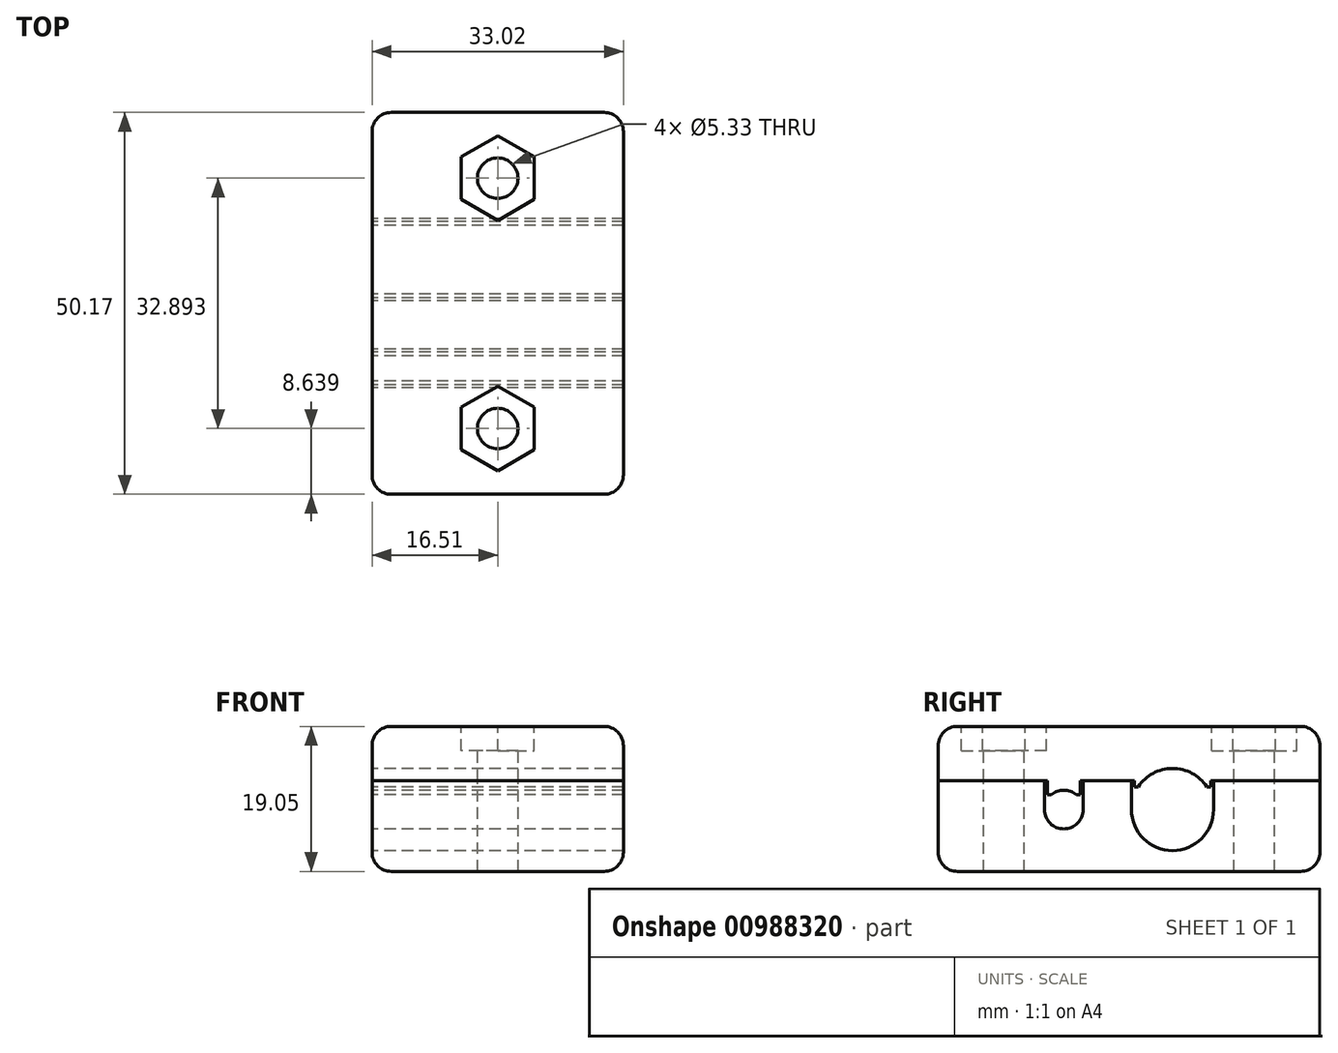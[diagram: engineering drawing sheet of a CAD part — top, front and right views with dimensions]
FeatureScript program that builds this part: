
annotation { "Feature Type Name" : "Feature", "Feature Type Description" : "" }
export const myFeature = defineFeature(function(context is Context, id is Id, definition is map)
    precondition{}
    {
        {
            var Q0;
            Q0=qCreatedBy(makeId("Right.planeOp"),FACE);
            var sketch = newSketch(context, id + "F0", { "sketchPlane" : qUnion([Q0])});
            skLineSegment(sketch, "E0", {"start": v(0, 10.92) * mm, "end": v(-30.8, 10.92) * mm});
            skLineSegment(sketch, "E1", {"start": v(-30.8, -8.13) * mm, "end": v(0, -8.13) * mm});
            skLineSegment(sketch, "E2", {"start": v(-30.8, 3.8) * mm, "end": v(-16.45, 3.8) * mm});
            skLineSegment(sketch, "E3", {"start": v(19.37, 3.81) * mm, "end": v(19.37, 10.92) * mm});
            skLineSegment(sketch, "E4", {"start": v(0, 10.92) * mm, "end": v(19.37, 10.92) * mm});
            skLineSegment(sketch, "E5", {"start": v(19.37, -8.13) * mm, "end": v(0, -8.13) * mm});
            skArc(sketch, "E6.trimOffspring", {"start": v(-5.4, 0) * mm, "mid": v(0, -5.4) * mm, "end": v(5.4, 0) * mm});
            skArc(sketch, "E7", {"start": v(-16.83, 0) * mm, "mid": v(-14.29, -2.54) * mm, "end": v(-11.75, 0) * mm});
            skLineSegment(sketch, "E8", {"start": v(5.4, 0) * mm, "end": v(5.4, 3.78) * mm});
            skLineSegment(sketch, "E9", {"start": v(5.4, 3.78) * mm, "end": v(19.37, 3.78) * mm});
            skLineSegment(sketch, "E10", {"start": v(19.37, 3.78) * mm, "end": v(19.37, -8.13) * mm});
            skLineSegment(sketch, "E11", {"start": v(-11.75, 0) * mm, "end": v(-11.75, 3.78) * mm});
            skLineSegment(sketch, "E12", {"start": v(-11.75, 3.78) * mm, "end": v(-5.4, 3.78) * mm});
            skLineSegment(sketch, "E13", {"start": v(-5.4, 3.78) * mm, "end": v(-5.4, 0) * mm});
            skLineSegment(sketch, "E14", {"start": v(-30.8, -8.13) * mm, "end": v(-30.8, 3.78) * mm});
            skLineSegment(sketch, "E15", {"start": v(-16.83, 0) * mm, "end": v(-16.83, 3.78) * mm});
            skLineSegment(sketch, "E16", {"start": v(-16.83, 3.78) * mm, "end": v(-30.8, 3.78) * mm});
            skLineSegment(sketch, "E17", {"start": v(-16.45, 3.8) * mm, "end": v(-16.45, 1.93) * mm});
            skLineSegment(sketch, "E18", {"start": v(-12.13, 1.93) * mm, "end": v(-12.13, 3.81) * mm});
            skLineSegment(sketch, "E19", {"start": v(-30.8, 3.8) * mm, "end": v(-30.8, 10.92) * mm});
            skLineSegment(sketch, "E20.trimOffspring", {"start": v(-12.13, 3.81) * mm, "end": v(-5.02, 3.81) * mm});
            skLineSegment(sketch, "E21.left", {"start": v(5.02, 3.81) * mm, "end": v(5.02, 3) * mm});
            skLineSegment(sketch, "E22.left", {"start": v(-5.02, 3.81) * mm, "end": v(-5.02, 3) * mm});
            skLineSegment(sketch, "E23.trimOffspring", {"start": v(5.02, 3.81) * mm, "end": v(19.37, 3.81) * mm});
            skLineSegment(sketch, "E24", {"start": v(5.02, 3) * mm, "end": v(4.5, 3) * mm});
            skLineSegment(sketch, "E25", {"start": v(-5.02, 3) * mm, "end": v(-4.5, 3) * mm});
            skArc(sketch, "E26", {"start": v(4.5, 3) * mm, "mid": v(0, 5.41) * mm, "end": v(-4.5, 3) * mm});
            skLineSegment(sketch, "E27", {"start": v(-12.13, 1.93) * mm, "end": v(-12.64, 1.93) * mm});
            skLineSegment(sketch, "E28", {"start": v(-16.45, 1.93) * mm, "end": v(-15.94, 1.93) * mm});
            skArc(sketch, "E29", {"start": v(-12.64, 1.93) * mm, "mid": v(-14.29, 2.54) * mm, "end": v(-15.94, 1.93) * mm});
            skSolve(sketch);
        }
        {
            var Q0;
            Q0=qSketchRegion(id+"F0",true);
            extrude(context, id + "F1", {"entities" : qUnion([Q0]), "depth" : 33.02 * mm, "offsetDistance" : 25.4 * mm});
        }
        {
            var Q0;
            Q0=makeQuery(id+"F1.opExtrude","SWEPT_FACE",FACE,{"disambiguationData":[OSD([sQuery(id+"F0.wireOp",EDGE,"E0"),sQuery(id+"F0.wireOp",EDGE,"E4")])]});
            var sketch = newSketch(context, id + "F2", { "sketchPlane" : qUnion([Q0])});
            skCircle(sketch, "E30", {"center": v(16.51, -22.16) * mm, "radius": 2.67 * mm});
            skPoint(sketch, "E30.centerSnap0", {"position": v(16.51, 19.37) * mm});
            skCircle(sketch, "E31", {"center": v(16.51, 10.73) * mm, "radius": 2.67 * mm});
            skSolve(sketch);
        }
        {
            var Q0;
            Q0=qSketchRegion(id+"F2",true);
            extrude(context, id + "F3", {"entities" : qUnion([Q0]), "operationType" : NewBodyOperationType.REMOVE, "oppositeDirection" : true, "depth" : 25.4 * mm, "offsetDistance" : 25.4 * mm});
        }
        {
            var Q0;
            Q0=makeQuery(id+"F1.opExtrude","SWEPT_FACE",FACE,{"disambiguationData":[OSD([sQuery(id+"F0.wireOp",EDGE,"E0"),sQuery(id+"F0.wireOp",EDGE,"E4")])]});
            var sketch = newSketch(context, id + "F4", { "sketchPlane" : qUnion([Q0])});
            skCircle(sketch, "E32.cCircle", {"center": v(16.51, -22.16) * mm, "radius": 4.83 * mm, "construction": true});
            skLineSegment(sketch, "E32.0", {"start": v(21.34, -19.38) * mm, "end": v(21.34, -24.95) * mm});
            skLineSegment(sketch, "E32.1", {"start": v(21.34, -24.95) * mm, "end": v(16.51, -27.73) * mm});
            skLineSegment(sketch, "E32.2", {"start": v(16.5, -27.73) * mm, "end": v(11.68, -24.95) * mm});
            skLineSegment(sketch, "E32.3", {"start": v(11.68, -24.95) * mm, "end": v(11.68, -19.38) * mm});
            skLineSegment(sketch, "E32.4", {"start": v(11.68, -19.38) * mm, "end": v(16.5, -16.59) * mm});
            skLineSegment(sketch, "E32.5", {"start": v(16.51, -16.59) * mm, "end": v(21.34, -19.38) * mm});
            skPoint(sketch, "E32.0.midPoint", {"position": v(21.34, -22.16) * mm});
            skLineSegment(sketch, "E33", {"start": v(33.02, -5.72) * mm, "end": v(5.36, -5.72) * mm, "construction": true});
            skPoint(sketch, "E34.MirrorP", {"position": v(21.34, 10.73) * mm});
            skLineSegment(sketch, "E35.MirrorCS", {"start": v(16.5, 16.3) * mm, "end": v(11.68, 13.52) * mm});
            skCircle(sketch, "E36.MirrorC", {"center": v(16.51, 10.73) * mm, "radius": 4.83 * mm, "construction": true});
            skLineSegment(sketch, "E37.MirrorCS", {"start": v(16.51, 5.16) * mm, "end": v(21.34, 7.95) * mm});
            skLineSegment(sketch, "E38.MirrorCS", {"start": v(11.68, 7.95) * mm, "end": v(16.5, 5.16) * mm});
            skLineSegment(sketch, "E39.MirrorCS", {"start": v(21.34, 7.95) * mm, "end": v(21.34, 13.52) * mm});
            skLineSegment(sketch, "E40.MirrorCS", {"start": v(21.34, 13.52) * mm, "end": v(16.5, 16.3) * mm});
            skLineSegment(sketch, "E41.MirrorCS", {"start": v(11.68, 13.52) * mm, "end": v(11.68, 7.95) * mm});
            skSolve(sketch);
        }
        {
            var Q0;
            Q0=qSketchRegion(id+"F4",true);
            extrude(context, id + "F5", {"entities" : qUnion([Q0]), "operationType" : NewBodyOperationType.REMOVE, "oppositeDirection" : true, "depth" : 3.17 * mm, "offsetDistance" : 25.4 * mm});
        }
        {
            var Q0;
            Q0=makeQuery(id+"F1.opExtrude","SWEPT_EDGE",EDGE,{"disambiguationData":[OSD([sQuery(id+"F0.wireOp",EDGE,"RtNWUVL0-efdT-tvqy-NiaK-mgzKuhDWmYlO"),sQuery(id+"F0.wireOp",EDGE,"E5")])]});
            var Q1;
            Q1=makeQuery(id+"F1.opExtrude","SWEPT_EDGE",EDGE,{"disambiguationData":[OSD([sQuery(id+"F0.wireOp",EDGE,"E3"),sQuery(id+"F0.wireOp",EDGE,"E4")])]});
            var Q2;
            Q2=makeQuery(id+"F1.opExtrude","CAP_EDGE",EDGE,{"disambiguationData":[OSD([sQuery(id+"F0.wireOp",EDGE,"E0"),sQuery(id+"F0.wireOp",EDGE,"E4")])],"isStart":true});
            var Q3;
            Q3=makeQuery(id+"F1.opExtrude","SWEPT_EDGE",EDGE,{"disambiguationData":[OSD([sQuery(id+"F0.wireOp",EDGE,"E0"),sQuery(id+"F0.wireOp",EDGE,"E19")])]});
            var Q4;
            Q4=makeQuery(id+"F1.opExtrude","CAP_EDGE",EDGE,{"disambiguationData":[OSD([sQuery(id+"F0.wireOp",EDGE,"E0"),sQuery(id+"F0.wireOp",EDGE,"E4")])],"isStart":false});
            var Q5;
            Q5=makeQuery(id+"F1.opExtrude","CAP_EDGE",EDGE,{"disambiguationData":[OSD([sQuery(id+"F0.wireOp",EDGE,"E1"),sQuery(id+"F0.wireOp",EDGE,"E5")])],"isStart":true});
            var Q6;
            Q6=makeQuery(id+"F1.opExtrude","SWEPT_EDGE",EDGE,{"disambiguationData":[OSD([sQuery(id+"F0.wireOp",EDGE,"E1"),sQuery(id+"F0.wireOp",EDGE,"E14")])]});
            var Q7;
            Q7=makeQuery(id+"F1.opExtrude","CAP_EDGE",EDGE,{"disambiguationData":[OSD([sQuery(id+"F0.wireOp",EDGE,"E14")])],"isStart":false});
            var Q8;
            Q8=makeQuery(id+"F1.opExtrude","CAP_EDGE",EDGE,{"disambiguationData":[OSD([sQuery(id+"F0.wireOp",EDGE,"E14")])],"isStart":true});
            var Q9;
            Q9=makeQuery(id+"F1.opExtrude","CAP_EDGE",EDGE,{"disambiguationData":[OSD([sQuery(id+"F0.wireOp",EDGE,"E10")])],"isStart":false});
            var Q10;
            Q10=makeQuery(id+"F1.opExtrude","CAP_EDGE",EDGE,{"disambiguationData":[OSD([sQuery(id+"F0.wireOp",EDGE,"E10")])],"isStart":true});
            var Q11;
            Q11=makeQuery(id+"F1.opExtrude","CAP_EDGE",EDGE,{"disambiguationData":[OSD([sQuery(id+"F0.wireOp",EDGE,"E3")])],"isStart":false});
            var Q12;
            Q12=makeQuery(id+"F1.opExtrude","CAP_EDGE",EDGE,{"disambiguationData":[OSD([sQuery(id+"F0.wireOp",EDGE,"E3")])],"isStart":true});
            var Q13;
            Q13=makeQuery(id+"F1.opExtrude","CAP_EDGE",EDGE,{"disambiguationData":[OSD([sQuery(id+"F0.wireOp",EDGE,"E19")])],"isStart":true});
            var Q14;
            Q14=makeQuery(id+"F1.opExtrude","CAP_EDGE",EDGE,{"disambiguationData":[OSD([sQuery(id+"F0.wireOp",EDGE,"E19")])],"isStart":false});
            var Q15;
            Q15=makeQuery(id+"F1.opExtrude","CAP_EDGE",EDGE,{"disambiguationData":[OSD([sQuery(id+"F0.wireOp",EDGE,"E1"),sQuery(id+"F0.wireOp",EDGE,"E5")])],"isStart":false});
            fillet(context, id + "F6", {"entities" : qUnion([Q0, Q1, Q2, Q3, Q4, Q5, Q6, Q7, Q8, Q9, Q10, Q11, Q12, Q13, Q14, Q15]), "radius" : 2.54 * mm, "tangentPropagation" : true, "allowEdgeOverflow" : false});
        }
    });
